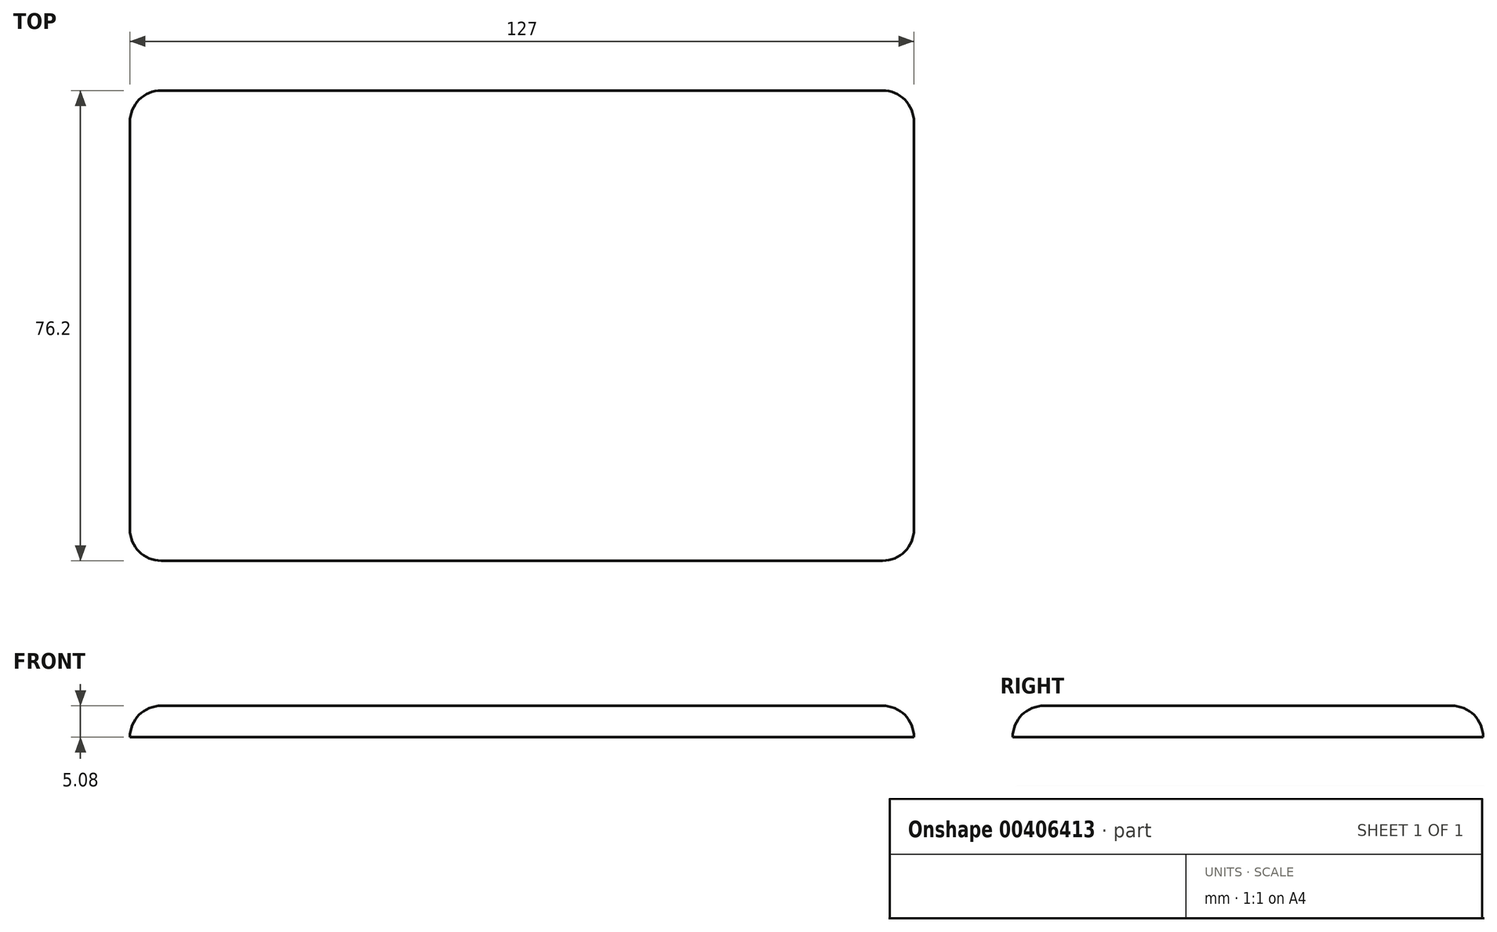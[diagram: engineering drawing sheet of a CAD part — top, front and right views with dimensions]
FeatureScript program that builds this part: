
annotation { "Feature Type Name" : "Feature", "Feature Type Description" : "" }
export const myFeature = defineFeature(function(context is Context, id is Id, definition is map)
    precondition{}
    {
        {
            var Q0;
            Q0=qCreatedBy(makeId("Top.planeOp"),FACE);
            var sketch = newSketch(context, id + "F0", { "sketchPlane" : qUnion([Q0])});
            skLineSegment(sketch, "E0.bottom", {"start": v(5.08, 76.2) * mm, "end": v(121.92, 76.2) * mm});
            skLineSegment(sketch, "E0.top", {"start": v(5.08, 0) * mm, "end": v(121.92, 0) * mm});
            skLineSegment(sketch, "E0.left", {"start": v(0, 71.12) * mm, "end": v(0, 5.08) * mm});
            skLineSegment(sketch, "E0.right", {"start": v(127, 71.12) * mm, "end": v(127, 5.08) * mm});
            skPoint(sketch, "E1.visualSharp", {"position": v(0, 76.2) * mm});
            skArc(sketch, "E1.filletArc", {"start": v(5.08, 76.2) * mm, "mid": v(1.49, 74.71) * mm, "end": v(0, 71.12) * mm});
            skPoint(sketch, "E2.visualSharp", {"position": v(127, 76.2) * mm});
            skArc(sketch, "E2.filletArc", {"start": v(127, 71.12) * mm, "mid": v(125.51, 74.71) * mm, "end": v(121.92, 76.2) * mm});
            skPoint(sketch, "E3.visualSharp", {"position": v(127, 0) * mm});
            skArc(sketch, "E3.filletArc", {"start": v(121.92, 0) * mm, "mid": v(125.51, 1.49) * mm, "end": v(127, 5.08) * mm});
            skPoint(sketch, "E4.visualSharp", {"position": v(0, 0) * mm});
            skArc(sketch, "E4.filletArc", {"start": v(0, 5.08) * mm, "mid": v(1.49, 1.49) * mm, "end": v(5.08, 0) * mm});
            skSolve(sketch);
        }
        {
            var Q0;
            Q0 = qSketchRegion(id + "F0", true);
            extrude(context, id + "F1", {"entities" : qUnion([Q0]), "depth" : 5.08 * mm});
        }
        {
            var Q0;
            Q0=makeQuery(id+"F1.opExtrude","CAP_FACE",FACE,{"disambiguationData":[OSD([sQuery(id+"F0.wireOp",EDGE,"E0.bottom"),sQuery(id+"F0.wireOp",EDGE,"E0.top"),sQuery(id+"F0.wireOp",EDGE,"E0.left"),sQuery(id+"F0.wireOp",EDGE,"E0.right"),sQuery(id+"F0.wireOp",EDGE,"E1.filletArc"),sQuery(id+"F0.wireOp",EDGE,"E2.filletArc"),sQuery(id+"F0.wireOp",EDGE,"E3.filletArc"),sQuery(id+"F0.wireOp",EDGE,"E4.filletArc")])],"isStart":false});
            fillet(context, id + "F2", {"entities" : qUnion([Q0]), "radius" : 5.08 * mm, "tangentPropagation" : true, "allowEdgeOverflow" : false});
        }
    });
